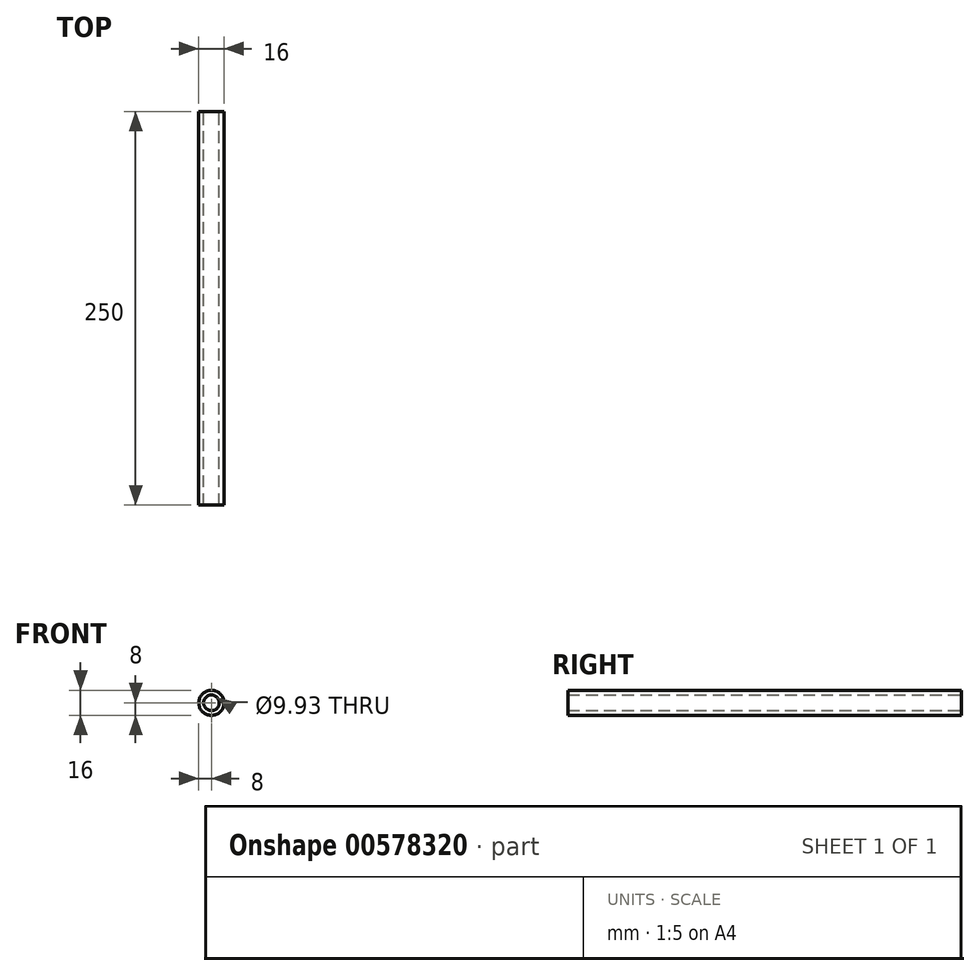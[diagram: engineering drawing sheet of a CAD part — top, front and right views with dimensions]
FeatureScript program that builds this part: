
annotation { "Feature Type Name" : "Feature", "Feature Type Description" : "" }
export const myFeature = defineFeature(function(context is Context, id is Id, definition is map)
    precondition{}
    {
        {
            var Q0;
            Q0=qCreatedBy(makeId("Front.planeOp"),FACE);
            var sketch = newSketch(context, id + "F0", { "sketchPlane" : qUnion([Q0])});
            skCircle(sketch, "E0", {"center": v(0, 0) * mm, "radius": 8 * mm});
            skCircle(sketch, "E1", {"center": v(0, 0) * mm, "radius": 4.97 * mm});
            skSolve(sketch);
        }
        {
            var Q0;
            Q0 = qSketchRegion(id + "F0", true);
            extrude(context, id + "F1", {"entities" : qUnion([Q0]), "depth" : 250 * mm, "offsetDistance" : 25 * mm});
        }
    });
